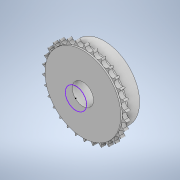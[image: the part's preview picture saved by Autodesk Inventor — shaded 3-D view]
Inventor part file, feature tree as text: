
AUTODESK INVENTOR PART (.ipt)
format: ipt  version: 2021 (Build 250183000, 183)  size: 515,072 bytes
history: native  units: in
note: dims shown in document units (in); Inventor stores cm internally (conversion verified against a paired STEP export)
features: sketch x6, extrude x3, hole x2, plane x1, mirror x1
ambient origin geometry x8: Origin, YZ Plane, XZ Plane, XY Plane, X Axis, Y Axis, Z Axis, Center Point
bodies: Solid1 (feature_tree)
feature tree (13):
  extrude  "Extrusion1"  Depth=0.3937in
  sketch  "Sketch2"  dims[d3=0.7874in d4=0.0in d5=-0.0787in]
  sketch  "Sketch3"  dims[d6=0.2362in d7=0.0in]
  extrude  "Extrusion2"  [1 undecoded]
  plane  "Work Plane1"
  sketch  "Sketch4"  dims[d8=1.1811in d9=0.2362in d10=0.119in d11=0.0787in d12=0.5635in d13=0.315in d14=0.8108in]
  sketch  "Sketch5"  dims[d15=1.1811in d16=0.2362in d17=0.119in d18=0.0787in d19=0.5635in d20=1.1024in d21=0.0in d22=0.0295in]
  extrude  "Extrusion3"  Depth=0.0295in
  hole  "Hole1"  [1 undecoded]
  hole  "Hole2"  [1 undecoded]
  mirror  "Mirror1"
  sketch  "Sketch1"  dims[d0=0.3937in d1=0.0in d2=3.937in]
  sketch  "Sketch6"  dims[d23=0.8108in d24=0.0025in d25=0.0295in d26=0.0148in]
note: 3 required parameter values undecoded (feature->parameter linkage not recoverable at this tier; creation-order binding heuristic only, values carry confidence <= 0.55)
